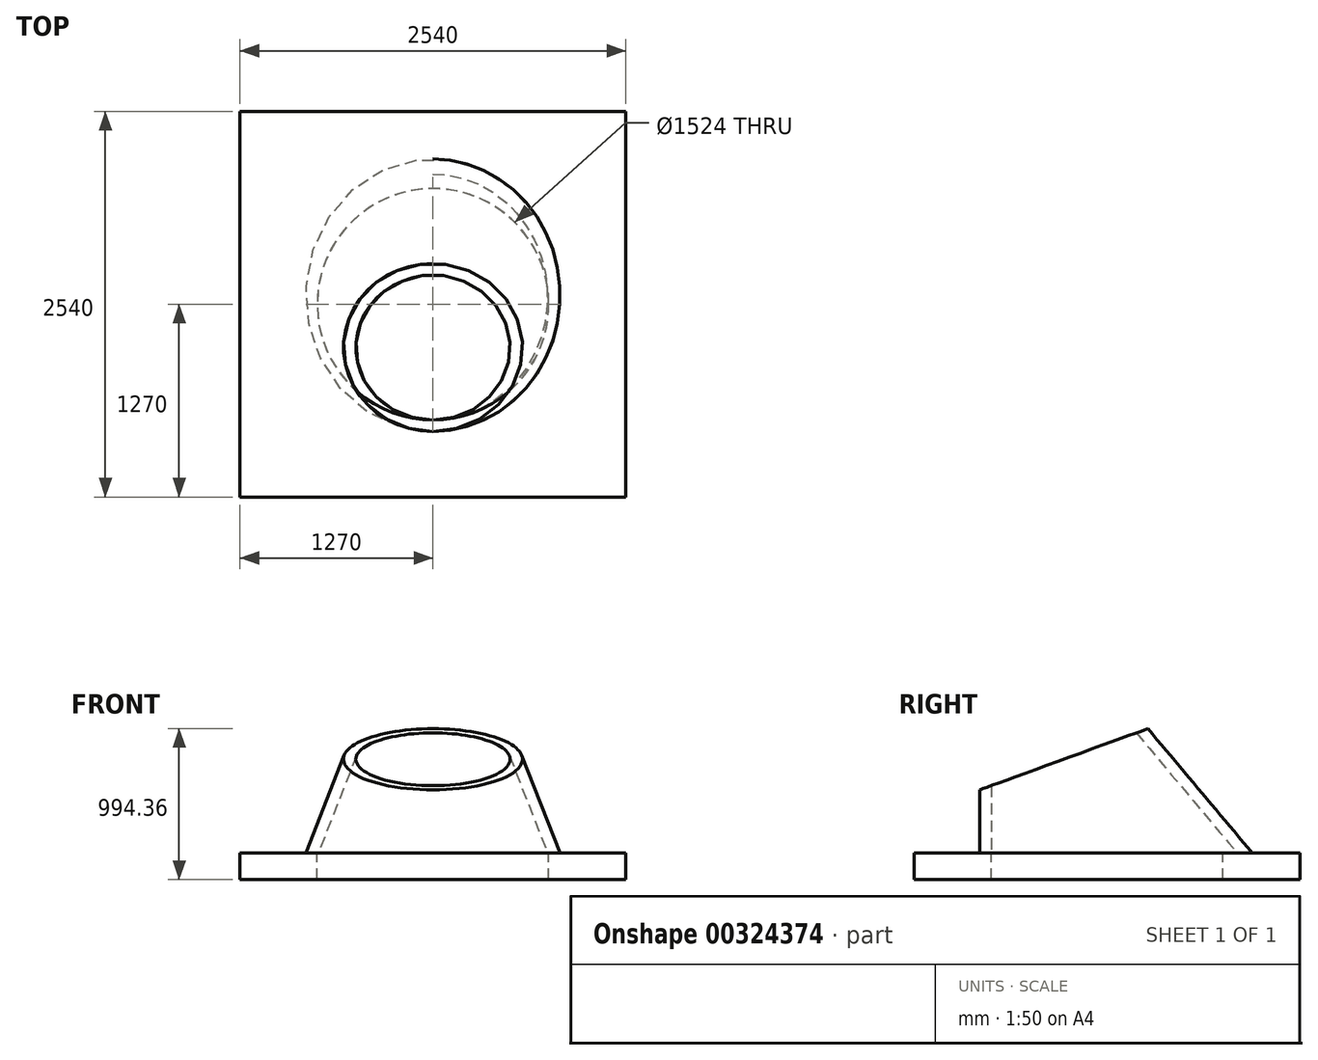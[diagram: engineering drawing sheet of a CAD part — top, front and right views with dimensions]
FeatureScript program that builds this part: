
annotation { "Feature Type Name" : "Feature", "Feature Type Description" : "" }
export const myFeature = defineFeature(function(context is Context, id is Id, definition is map)
    precondition{}
    {
        {
            var Q0;
            Q0=qCreatedBy(makeId("Top.planeOp"),FACE);
            var sketch = newSketch(context, id + "F0", { "sketchPlane" : qUnion([Q0])});
            skCircle(sketch, "E0", {"center": v(0, 0) * mm, "radius": 762 * mm});
            skPoint(sketch, "E1", {"position": v(0, -762) * mm});
            skSolve(sketch);
        }
        {
            var Q0;
            Q0=qCreatedBy(makeId("Top.planeOp"),FACE);
            cPlane(context, id + "F1", {"entities" : qUnion([Q0]), "cplaneType" : CPlaneType.OFFSET, "offset" : 444.5 * mm, "width" : 152.4 * mm, "height" : 152.4 * mm});
        }
        {
            var Q0;
            Q0=qCreatedBy(id+"F1.planeOp",FACE);
            var sketch = newSketch(context, id + "F2", { "sketchPlane" : qUnion([Q0])});
            skPoint(sketch, "E2.0", {"position": v(0, -762) * mm});
            skLineSegment(sketch, "E3", {"start": v(0, -762) * mm, "end": v(855.43, -762) * mm, "construction": true});
            skSolve(sketch);
        }
        {
            var Q0;
            Q0=sQuery(id+"F2.wireOp",EDGE,"E3");
            cPlane(context, id + "F3", {"entities" : qUnion([Q0]), "cplaneType" : CPlaneType.LINE_ANGLE, "offset" : 25.4 * mm, "angle" : 110 * degree, "width" : 152.4 * mm, "height" : 152.4 * mm});
        }
        {
            var Q0;
            Q0=qCreatedBy(id+"F3.planeOp",FACE);
            var sketch = newSketch(context, id + "F4", { "sketchPlane" : qUnion([Q0])});
            skLineSegment(sketch, "E4", {"start": v(0, -220.73) * mm, "end": v(0, 299.74) * mm, "construction": true});
            skLineSegment(sketch, "E5", {"start": v(0, -220.73) * mm, "end": v(0, -353.23) * mm, "construction": true});
            skPoint(sketch, "E6", {"position": v(0, -630.7) * mm});
            skPoint(sketch, "E7", {"position": v(0, -662.44) * mm});
            skCircle(sketch, "E8", {"center": v(0, -56.02) * mm, "radius": 606.43 * mm});
            skCircle(sketch, "E9", {"center": v(0, -56.02) * mm, "radius": 523.88 * mm});
            skSolve(sketch);
        }
        {
            var Q0;
            Q0=qCreatedBy(makeId("Right.planeOp"),FACE);
            var sketch = newSketch(context, id + "F5", { "sketchPlane" : qUnion([Q0])});
            skPoint(sketch, "E10.0", {"position": v(-762, 0) * mm});
            skPoint(sketch, "E11.0", {"position": v(-762, 444.5) * mm});
            skLineSegment(sketch, "E12", {"start": v(-762, 0) * mm, "end": v(-762, 444.5) * mm});
            skLineSegment(sketch, "E13.0", {"start": v(-838.2, 0) * mm, "end": v(-838.2, 416.77) * mm});
            skLineSegment(sketch, "E14.0", {"start": v(-776.92, 439.07) * mm, "end": v(207.65, 797.42) * mm});
            skLineSegment(sketch, "E15.0", {"start": v(-854.49, 410.84) * mm, "end": v(285.22, 825.66) * mm});
            skLineSegment(sketch, "E16.0", {"start": v(-776.92, 439.07) * mm, "end": v(207.65, 797.42) * mm, "construction": true});
            skLineSegment(sketch, "E17.0", {"start": v(-854.49, 410.84) * mm, "end": v(285.22, 825.66) * mm, "construction": true});
            skLineSegment(sketch, "E18", {"start": v(-762, 0) * mm, "end": v(-838.2, 0) * mm});
            skPoint(sketch, "E19.0", {"position": v(-284.64, 618.25) * mm});
            skLineSegment(sketch, "E20", {"start": v(-284.64, 618.25) * mm, "end": v(-59.61, 0) * mm, "construction": true});
            skLineSegment(sketch, "E21.MirrorCS", {"start": v(478.45, 451.49) * mm, "end": v(192.73, 792) * mm});
            skLineSegment(sketch, "E22.MirrorCS", {"start": v(536.82, 500.47) * mm, "end": v(268.93, 819.73) * mm});
            skLineSegment(sketch, "E23", {"start": v(285.22, 825.66) * mm, "end": v(296.08, 795.82) * mm});
            skLineSegment(sketch, "E24", {"start": v(-854.49, 410.84) * mm, "end": v(-843.63, 381) * mm});
            skLineSegment(sketch, "E25.0", {"start": v(-762, 0) * mm, "end": v(762, 0) * mm, "construction": true});
            skLineSegment(sketch, "E26", {"start": v(762, 0) * mm, "end": v(1161.95, 0) * mm, "construction": true});
            skLineSegment(sketch, "E27", {"start": v(478.45, 451.49) * mm, "end": v(857.29, 0) * mm});
            skLineSegment(sketch, "E28", {"start": v(536.82, 500.47) * mm, "end": v(956.76, 0) * mm});
            skLineSegment(sketch, "E29", {"start": v(956.76, 0) * mm, "end": v(857.29, 0) * mm});
            skSolve(sketch);
        }
        {
            var Q0;
            {var subQ1=sQuery(id+"F5.wireOp",EDGE,"E21.MirrorCS");Q0=makeQuery(id+"F5.imprint","IMPRINT",FACE,{"disambiguationData":[TD([[makeQuery(id+"F5.imprint","IMPRINT",EDGE,{"derivedFrom":subQ1}),-1.0]])]});}
            var Q1;
            Q1=sQuery(id+"F5.wireOp",EDGE,"E20");
            revolve(context, id + "F6", {"entities" : qUnion([Q0]), "axis" : qUnion([Q1]), "revolveType" : RevolveType.FULL});
        }
        {
            var Q0;
            Q0=qCreatedBy(makeId("Front.planeOp"),FACE);
            var sketch = newSketch(context, id + "F7", { "sketchPlane" : qUnion([Q0])});
            skLineSegment(sketch, "E30.0", {"start": v(-762, 0) * mm, "end": v(762, 0) * mm});
            skLineSegment(sketch, "E31", {"start": v(-762, 0) * mm, "end": v(-3048, 0) * mm});
            skLineSegment(sketch, "E32", {"start": v(-762, 0) * mm, "end": v(4572, 0) * mm});
            skLineSegment(sketch, "E33.bottom", {"start": v(-3048, 0) * mm, "end": v(4572, 0) * mm});
            skLineSegment(sketch, "E33.top", {"start": v(-3048, -2540) * mm, "end": v(4572, -2540) * mm});
            skLineSegment(sketch, "E33.left", {"start": v(-3048, 0) * mm, "end": v(-3048, -2540) * mm});
            skLineSegment(sketch, "E33.right", {"start": v(4572, 0) * mm, "end": v(4572, -2540) * mm});
            skSolve(sketch);
        }
        {
            var Q0;
            Q0 = qSketchRegion(id + "F7", true);
            extrude(context, id + "F8", {"entities" : qUnion([Q0]), "operationType" : NewBodyOperationType.REMOVE, "endBound" : BoundingType.THROUGH_ALL, "oppositeDirection" : true, "depth" : 25.4 * mm, "hasSecondDirection" : true, "secondDirectionBound" : SecondDirectionBoundingType.THROUGH_ALL, "secondDirectionOppositeDirection" : false, "secondDirectionDepth" : 25.4 * mm});
        }
        {
            var Q0;
            Q0=qCreatedBy(makeId("Top.planeOp"),FACE);
            var sketch = newSketch(context, id + "F9", { "sketchPlane" : qUnion([Q0])});
            skCircle(sketch, "E34.0", {"center": v(0, 0) * mm, "radius": 762 * mm});
            skPoint(sketch, "E34.1", {"position": v(0, -762) * mm});
            skLineSegment(sketch, "E35.bottom", {"start": v(-1270, -1270) * mm, "end": v(1270, -1270) * mm});
            skLineSegment(sketch, "E35.top", {"start": v(-1270, 1270) * mm, "end": v(1270, 1270) * mm});
            skLineSegment(sketch, "E35.left", {"start": v(-1270, -1270) * mm, "end": v(-1270, 1270) * mm});
            skLineSegment(sketch, "E35.right", {"start": v(1270, -1270) * mm, "end": v(1270, 1270) * mm});
            skSolve(sketch);
        }
        {
            var Q0;
            Q0=makeQuery(id+"F9.imprint","IMPRINT",FACE,{"disambiguationData":[TD([[makeQuery(id+"F9.imprint","IMPRINT",EDGE,{"derivedFrom":sQuery(id+"F9.wireOp",EDGE,"E34.0")}),-1.0]])]});
            extrude(context, id + "F10", {"entities" : qUnion([Q0]), "oppositeDirection" : true, "depth" : 174.62 * mm});
        }
    });
